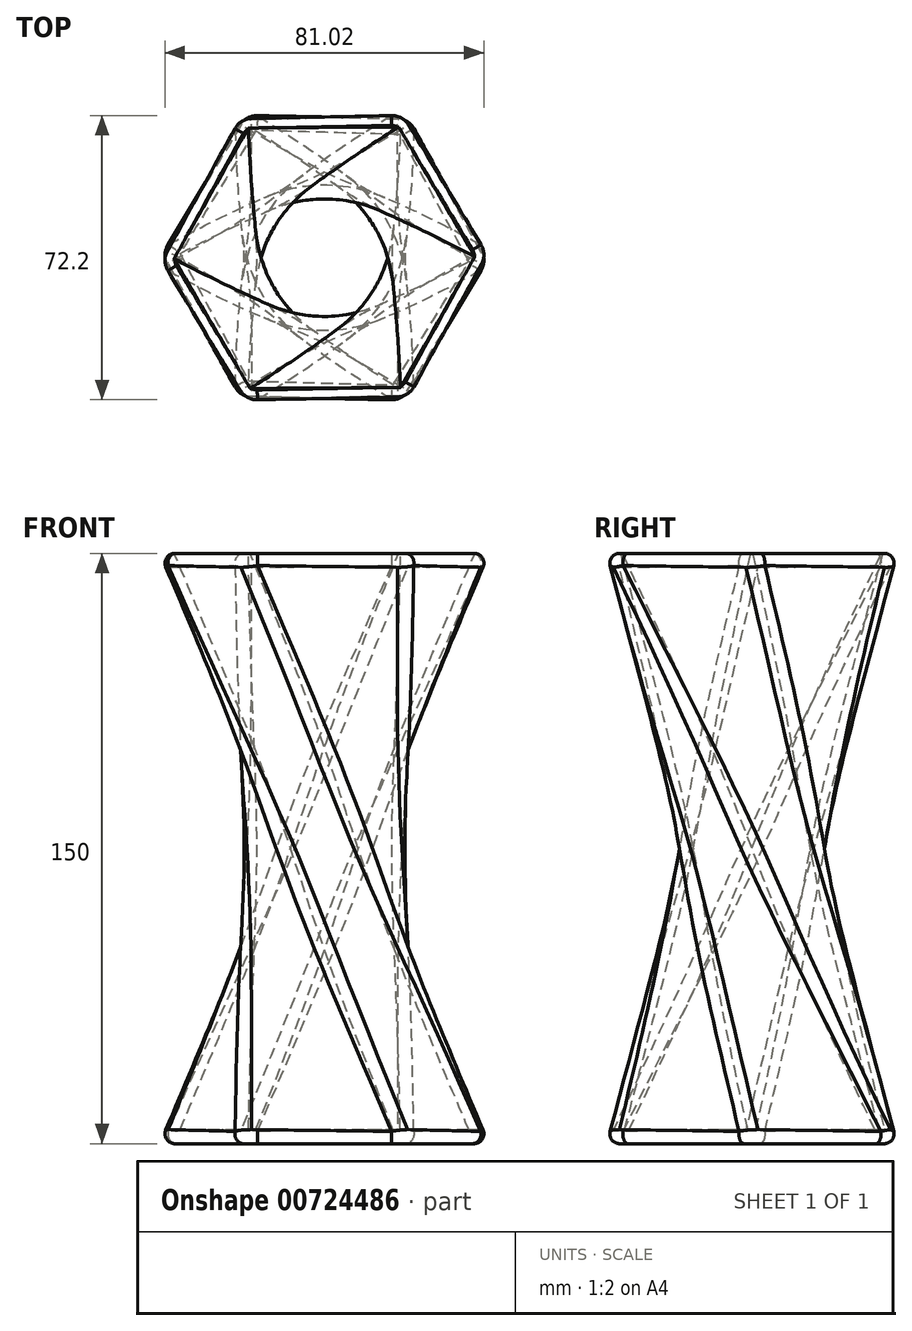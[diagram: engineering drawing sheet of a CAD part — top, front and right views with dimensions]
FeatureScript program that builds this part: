
annotation { "Feature Type Name" : "Feature", "Feature Type Description" : "" }
export const myFeature = defineFeature(function(context is Context, id is Id, definition is map)
    precondition{}
    {
        {
            var Q0;
            Q0=qCreatedBy(makeId("Top.planeOp"),FACE);
            var sketch = newSketch(context, id + "F0", { "sketchPlane" : qUnion([Q0])});
            skLineSegment(sketch, "E0", {"start": v(-43.65, 0) * mm, "end": v(41.43, 0) * mm, "construction": true});
            skLineSegment(sketch, "E1", {"start": v(0, 36.84) * mm, "end": v(0, -39.6) * mm, "construction": true});
            skLineSegment(sketch, "E2", {"start": v(-43.65, 0) * mm, "end": v(-22.38, 36.84) * mm});
            skLineSegment(sketch, "E3", {"start": v(-22.38, 36.84) * mm, "end": v(20.16, 36.84) * mm});
            skLineSegment(sketch, "E4", {"start": v(20.16, 36.84) * mm, "end": v(41.43, 0) * mm});
            skLineSegment(sketch, "E5.MirrorCS", {"start": v(-43.65, 0) * mm, "end": v(-22.38, -36.84) * mm});
            skLineSegment(sketch, "E6.MirrorCS", {"start": v(-22.38, -36.84) * mm, "end": v(20.16, -36.84) * mm});
            skLineSegment(sketch, "E7.MirrorCS", {"start": v(20.16, -36.84) * mm, "end": v(41.43, 0) * mm});
            skSolve(sketch);
        }
        {
            var Q0;
            Q0=qCreatedBy(makeId("Top.planeOp"),FACE);
            cPlane(context, id + "F1", {"entities" : qUnion([Q0]), "cplaneType" : CPlaneType.OFFSET, "offset" : 150 * mm, "width" : 150 * mm, "height" : 150 * mm});
        }
        {
            var Q0;
            Q0=qCreatedBy(id+"F1.planeOp",FACE);
            var sketch = newSketch(context, id + "F2", { "sketchPlane" : qUnion([Q0])});
            skLineSegment(sketch, "E8.0.0", {"start": v(-22.38, -36.84) * mm, "end": v(20.16, -36.84) * mm});
            skLineSegment(sketch, "E8.0.1", {"start": v(20.16, -36.84) * mm, "end": v(41.43, 0) * mm});
            skLineSegment(sketch, "E8.0.2", {"start": v(41.43, 0) * mm, "end": v(20.16, 36.84) * mm});
            skLineSegment(sketch, "E8.0.3", {"start": v(20.16, 36.84) * mm, "end": v(-22.38, 36.84) * mm});
            skLineSegment(sketch, "E8.0.4", {"start": v(-22.38, 36.84) * mm, "end": v(-43.65, 0) * mm});
            skLineSegment(sketch, "E8.0.5", {"start": v(-43.65, 0) * mm, "end": v(-22.38, -36.84) * mm});
            skSolve(sketch);
        }
        {
            var Q0;
            Q0=makeQuery(id+"F0.imprint","IMPRINT",FACE,{"disambiguationData":[TD([[makeQuery(id+"F0.imprint","IMPRINT",EDGE,{"derivedFrom":sQuery(id+"F0.wireOp",EDGE,"E2")}),-1.0]])]});
            var Q1;
            Q1=makeQuery(id+"F2.imprint","IMPRINT",FACE,{"disambiguationData":[TD([[makeQuery(id+"F2.imprint","IMPRINT",EDGE,{"derivedFrom":sQuery(id+"F2.wireOp",EDGE,"E8.0.0")}),1.0]])]});
            var Q2;
            Q2=sQuery(id+"F0.wireOp",VERTEX,"E3.end");
            var Q3;
            Q3=sQuery(id+"F2.wireOp",VERTEX,"E8.0.0.end");
            loft(context, id + "F3", {"sheetProfilesArray" : [{ "sheetProfileEntities" : qUnion([Q0]) }, { "sheetProfileEntities" : qUnion([Q1]) }], "matchConnections" : true, "connections" : [{ "connectionEntities" : qUnion([Q2, Q3]), "connectionEdgeQueries" : qUnion([]), "connectionEdgeParameters" : [] }]});
        }
        {
            var Q0;
            Q0=makeQuery(id+"F3.opLoft","CAP_FACE",FACE,{"disambiguationData":[OSD([makeQuery(id+"F2.imprint","IMPRINT",FACE,{"disambiguationData":[TD([[makeQuery(id+"F2.imprint","IMPRINT",EDGE,{"derivedFrom":sQuery(id+"F2.wireOp",EDGE,"E8.0.0")}),1.0]])]})])],"isStart":true});
            shell(context, id + "F4", {"entities" : qUnion([Q0]), "thickness" : 3.5 * mm});
        }
        {
            var Q0;
            Q0=makeQuery(id+"F3.opLoft","SWEPT_EDGE",EDGE,{"disambiguationData":[OSD([sQuery(id+"F0.wireOp",EDGE,"E4"),sQuery(id+"F0.wireOp",EDGE,"E7.MirrorCS"),sQuery(id+"F2.wireOp",EDGE,"E8.0.0"),sQuery(id+"F2.wireOp",EDGE,"E8.0.5")])]});
            var Q1;
            Q1=makeQuery(id+"F3.opLoft","SWEPT_EDGE",EDGE,{"disambiguationData":[OSD([sQuery(id+"F0.wireOp",EDGE,"E3"),sQuery(id+"F0.wireOp",EDGE,"E4"),sQuery(id+"F2.wireOp",EDGE,"E8.0.0"),sQuery(id+"F2.wireOp",EDGE,"E8.0.1")])]});
            var Q2;
            Q2=makeQuery(id+"F3.opLoft","SWEPT_EDGE",EDGE,{"disambiguationData":[OSD([sQuery(id+"F0.wireOp",EDGE,"E2"),sQuery(id+"F0.wireOp",EDGE,"E3"),sQuery(id+"F2.wireOp",EDGE,"E8.0.1"),sQuery(id+"F2.wireOp",EDGE,"E8.0.2")])]});
            var Q3;
            Q3=makeQuery(id+"F3.opLoft","SWEPT_EDGE",EDGE,{"disambiguationData":[OSD([sQuery(id+"F0.wireOp",EDGE,"E2"),sQuery(id+"F0.wireOp",EDGE,"E5.MirrorCS"),sQuery(id+"F2.wireOp",EDGE,"E8.0.2"),sQuery(id+"F2.wireOp",EDGE,"E8.0.3")])]});
            var Q4;
            Q4=makeQuery(id+"F3.opLoft","SWEPT_EDGE",EDGE,{"disambiguationData":[OSD([sQuery(id+"F0.wireOp",EDGE,"E5.MirrorCS"),sQuery(id+"F0.wireOp",EDGE,"E6.MirrorCS"),sQuery(id+"F2.wireOp",EDGE,"E8.0.3"),sQuery(id+"F2.wireOp",EDGE,"E8.0.4")])]});
            var Q5;
            Q5=makeQuery(id+"F3.opLoft","SWEPT_EDGE",EDGE,{"disambiguationData":[OSD([sQuery(id+"F0.wireOp",EDGE,"E6.MirrorCS"),sQuery(id+"F0.wireOp",EDGE,"E7.MirrorCS"),sQuery(id+"F2.wireOp",EDGE,"E8.0.4"),sQuery(id+"F2.wireOp",EDGE,"E8.0.5")])]});
            fillet(context, id + "F5", {"entities" : qUnion([Q0, Q1, Q2, Q3, Q4, Q5]), "radius" : 5 * mm, "tangentPropagation" : true, "allowEdgeOverflow" : false});
        }
        {
            var Q0;
            Q0=makeQuery(id+"F3.opLoft","MID_CAP_EDGE",EDGE,{"disambiguationData":[OSD([sQuery(id+"F2.wireOp",EDGE,"E8.0.0"),sQuery(id+"F2.wireOp",EDGE,"E8.0.4"),sQuery(id+"F2.wireOp",EDGE,"E8.0.5")])],"capPos":1.0});
            fillet(context, id + "F6", {"entities" : qUnion([Q0]), "radius" : 2.5 * mm, "tangentPropagation" : true, "allowEdgeOverflow" : false});
        }
        {
            var Q0;
            Q0=makeQuery(id+"F3.opLoft","CAP_FACE",FACE,{"disambiguationData":[OSD([makeQuery(id+"F0.imprint","IMPRINT",FACE,{"disambiguationData":[TD([[makeQuery(id+"F0.imprint","IMPRINT",EDGE,{"derivedFrom":sQuery(id+"F0.wireOp",EDGE,"E2")}),-1.0]])]})])],"isStart":true});
            fillet(context, id + "F7", {"entities" : qUnion([Q0]), "radius" : 2.5 * mm, "tangentPropagation" : true, "allowEdgeOverflow" : false});
        }
    });
